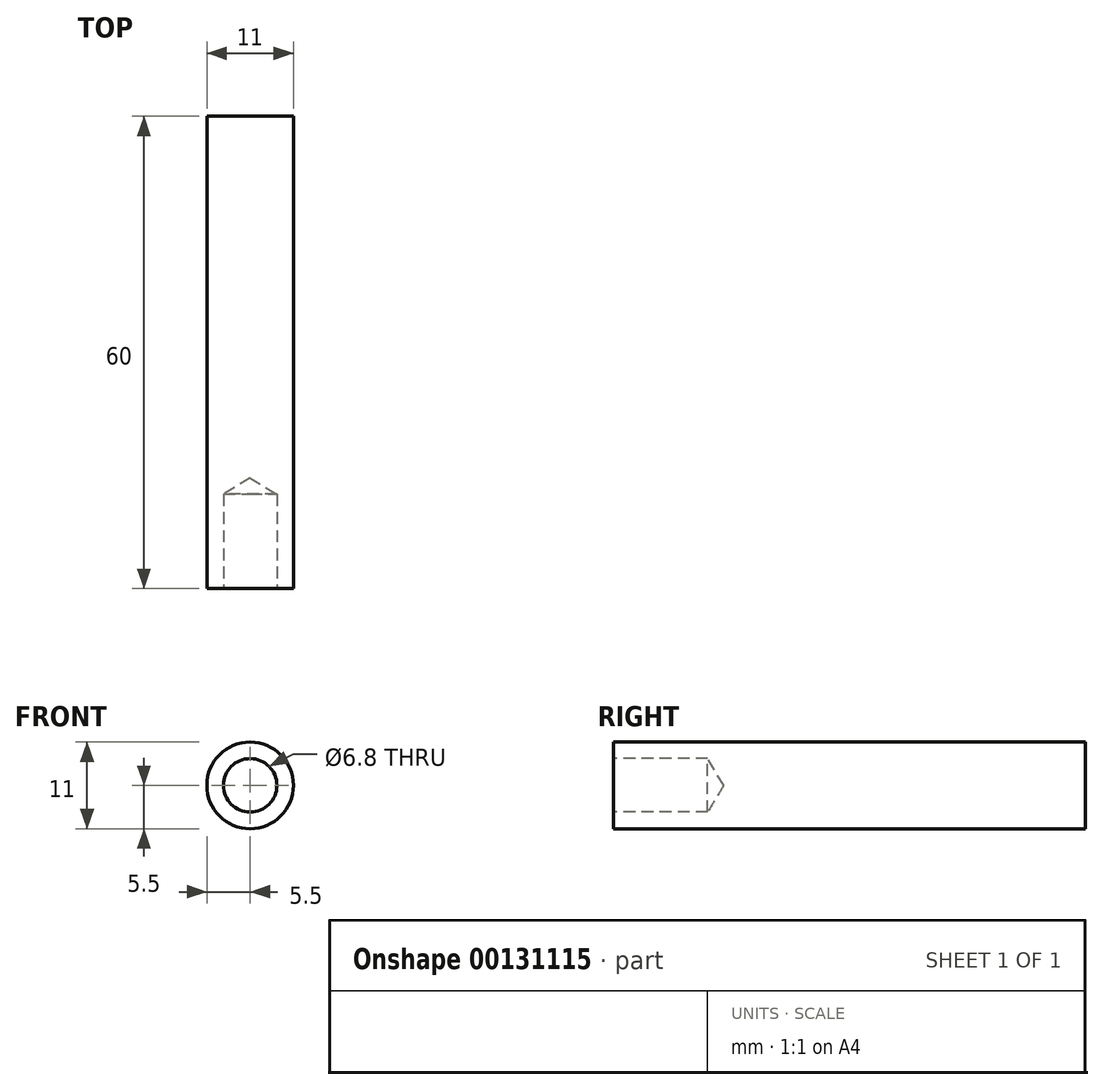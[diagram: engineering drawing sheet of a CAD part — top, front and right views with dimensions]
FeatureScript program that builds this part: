
annotation { "Feature Type Name" : "Feature", "Feature Type Description" : "" }
export const myFeature = defineFeature(function(context is Context, id is Id, definition is map)
    precondition{}
    {
        {
            var Q0;
            Q0=qCreatedBy(makeId("Front.planeOp"),FACE);
            var sketch = newSketch(context, id + "F0", { "sketchPlane" : qUnion([Q0])});
            skCircle(sketch, "E0", {"center": v(0, 0) * mm, "radius": 5.5 * mm});
            skSolve(sketch);
        }
        {
            var Q0;
            Q0 = qSketchRegion(id + "F0", true);
            extrude(context, id + "F1", {"entities" : qUnion([Q0]), "depth" : 60 * mm});
        }
        {
            var Q0;
            Q0=makeQuery(id+"F1.opExtrude","CAP_FACE",FACE,{"disambiguationData":[OSD([sQuery(id+"F0.wireOp",EDGE,"E0")])],"isStart":false});
            var sketch = newSketch(context, id + "F2", { "sketchPlane" : qUnion([Q0])});
            skPoint(sketch, "E1", {"position": v(0, 0) * mm});
            skSolve(sketch);
        }
        {
            var Q0;
            Q0=sQuery(id+"F2.wireOp",VERTEX,"E1");
            var Q1;
            Q1=makeQuery(id+"F1.opExtrude","SWEPT_BODY",BODY,{"disambiguationData":[OSD([sQuery(id+"F0.wireOp",EDGE,"E0")])]});
            hole(context, id + "F3", {"style" : HoleStyle.SIMPLE, "endStyle" : HoleEndStyle.BLIND, "holeDiameter" : 6.8 * mm, "holeDepth" : 12 * mm, "locations" : qUnion([Q0]), "scope" : qUnion([Q1])});
        }
    });
